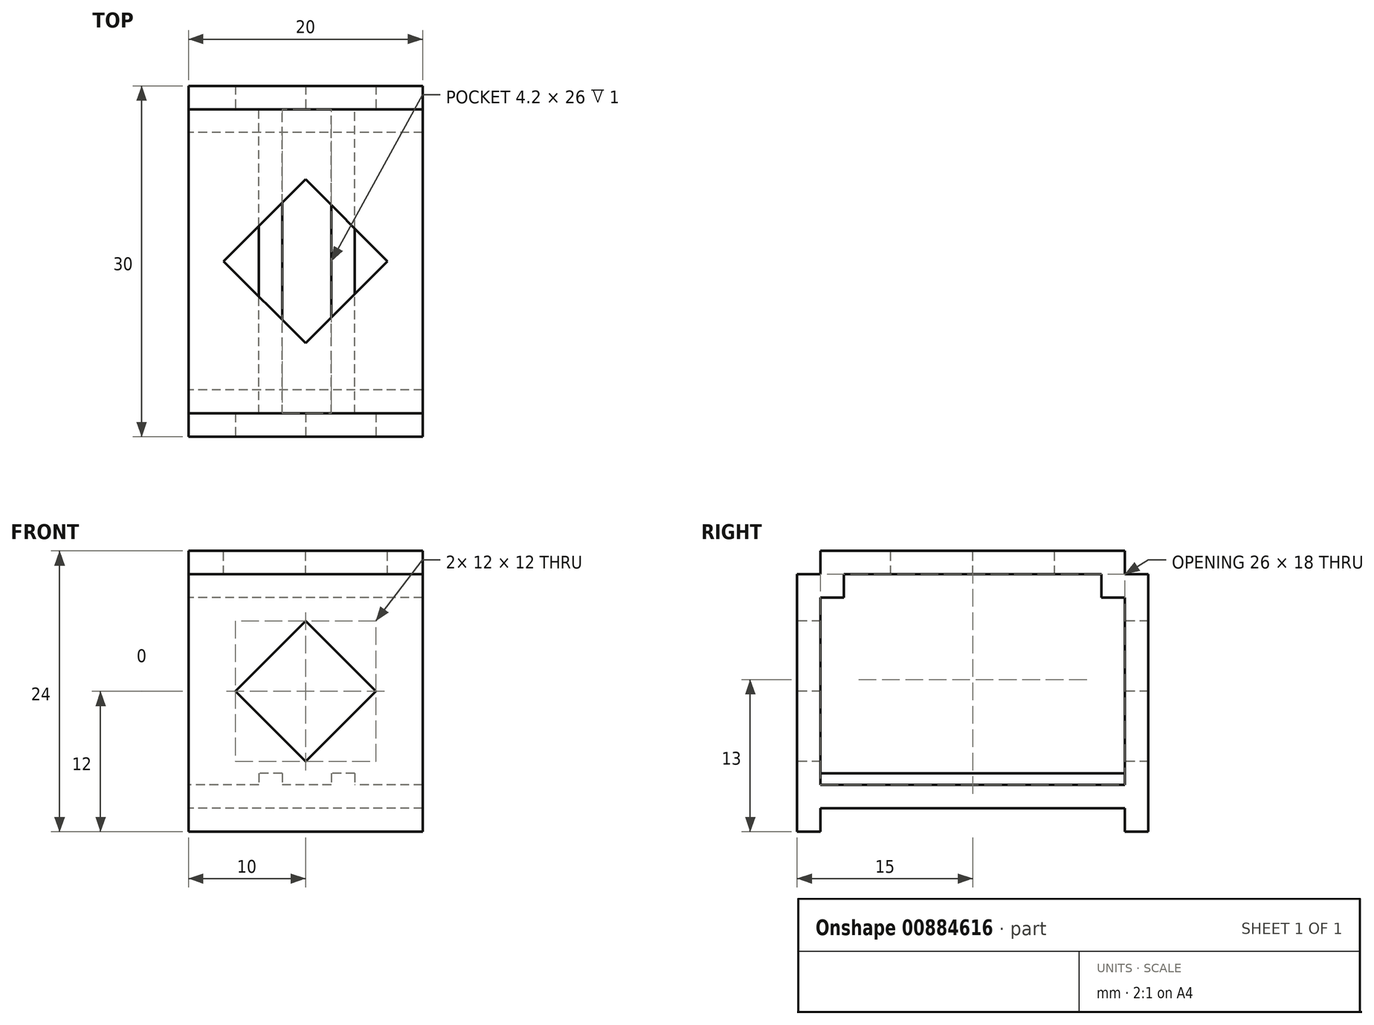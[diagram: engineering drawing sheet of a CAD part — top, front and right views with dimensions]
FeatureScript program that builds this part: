
annotation { "Feature Type Name" : "Feature", "Feature Type Description" : "" }
export const myFeature = defineFeature(function(context is Context, id is Id, definition is map)
    precondition{}
    {
        {
            var Q0;
            Q0=qCreatedBy(makeId("Right.planeOp"),FACE);
            var sketch = newSketch(context, id + "F0", { "sketchPlane" : qUnion([Q0])});
            skLineSegment(sketch, "E0", {"start": v(-13, 0) * mm, "end": v(13, 0) * mm});
            skLineSegment(sketch, "E1", {"start": v(13, 0) * mm, "end": v(13, -2) * mm});
            skLineSegment(sketch, "E2", {"start": v(13, -2) * mm, "end": v(15, -2) * mm});
            skLineSegment(sketch, "E3", {"start": v(15, -2) * mm, "end": v(15, 20) * mm});
            skLineSegment(sketch, "E4", {"start": v(15, 20) * mm, "end": v(13, 20) * mm});
            skLineSegment(sketch, "E5", {"start": v(13, 20) * mm, "end": v(13, 22) * mm});
            skLineSegment(sketch, "E6", {"start": v(13, 22) * mm, "end": v(-13, 22) * mm});
            skLineSegment(sketch, "E7", {"start": v(-13, 22) * mm, "end": v(-13, 20) * mm});
            skLineSegment(sketch, "E8", {"start": v(-13, 20) * mm, "end": v(-15, 20) * mm});
            skLineSegment(sketch, "E9", {"start": v(-15, 20) * mm, "end": v(-15, -2) * mm});
            skLineSegment(sketch, "E10", {"start": v(-15, -2) * mm, "end": v(-13, -2) * mm});
            skLineSegment(sketch, "E11", {"start": v(-13, -2) * mm, "end": v(-13, 0) * mm});
            skSolve(sketch);
        }
        {
            var Q0;
            Q0=makeQuery(id+"F0.imprint","IMPRINT",FACE,{"disambiguationData":[TD([[makeQuery(id+"F0.imprint","IMPRINT",EDGE,{"derivedFrom":sQuery(id+"F0.wireOp",EDGE,"E0")}),1.0]])]});
            extrude(context, id + "F1", {"entities" : qUnion([Q0]), "depth" : 20 * mm, "offsetDistance" : 25 * mm});
        }
        {
            var Q0;
            Q0=makeQuery(id+"F1.opExtrude","CAP_FACE",FACE,{"disambiguationData":[OSD([sQuery(id+"F0.wireOp",EDGE,"E0"),sQuery(id+"F0.wireOp",EDGE,"E1"),sQuery(id+"F0.wireOp",EDGE,"E2"),sQuery(id+"F0.wireOp",EDGE,"E3"),sQuery(id+"F0.wireOp",EDGE,"E4"),sQuery(id+"F0.wireOp",EDGE,"E5"),sQuery(id+"F0.wireOp",EDGE,"E6"),sQuery(id+"F0.wireOp",EDGE,"E7"),sQuery(id+"F0.wireOp",EDGE,"E8"),sQuery(id+"F0.wireOp",EDGE,"E9"),sQuery(id+"F0.wireOp",EDGE,"E10"),sQuery(id+"F0.wireOp",EDGE,"E11")])],"isStart":true});
            var Q1;
            Q1=makeQuery(id+"F1.opExtrude","CAP_FACE",FACE,{"disambiguationData":[OSD([sQuery(id+"F0.wireOp",EDGE,"E0"),sQuery(id+"F0.wireOp",EDGE,"E1"),sQuery(id+"F0.wireOp",EDGE,"E2"),sQuery(id+"F0.wireOp",EDGE,"E3"),sQuery(id+"F0.wireOp",EDGE,"E4"),sQuery(id+"F0.wireOp",EDGE,"E5"),sQuery(id+"F0.wireOp",EDGE,"E6"),sQuery(id+"F0.wireOp",EDGE,"E7"),sQuery(id+"F0.wireOp",EDGE,"E8"),sQuery(id+"F0.wireOp",EDGE,"E9"),sQuery(id+"F0.wireOp",EDGE,"E10"),sQuery(id+"F0.wireOp",EDGE,"E11")])],"isStart":false});
            shell(context, id + "F2", {"entities" : qUnion([Q0, Q1]), "thickness" : 2 * mm});
        }
        {
            var Q0;
            Q0=makeQuery(id+"F2.opShell","OFFSET_FACE",FACE,{"disambiguationData":[OSD([sQuery(id+"F0.wireOp",EDGE,"E3")])]});
            var sketch = newSketch(context, id + "F3", { "sketchPlane" : qUnion([Q0])});
            skLineSegment(sketch, "E12.bottom", {"start": v(8, 3) * mm, "end": v(6, 3) * mm});
            skLineSegment(sketch, "E12.top", {"start": v(8, 2) * mm, "end": v(6, 2) * mm});
            skLineSegment(sketch, "E12.left", {"start": v(8, 3) * mm, "end": v(8, 2) * mm});
            skLineSegment(sketch, "E12.right", {"start": v(6, 3) * mm, "end": v(6, 2) * mm});
            skLineSegment(sketch, "E13.1.0.0", {"start": v(14.2, 3) * mm, "end": v(12.2, 3) * mm});
            skLineSegment(sketch, "E13.1.0.1", {"start": v(14.2, 3) * mm, "end": v(14.2, 2) * mm});
            skLineSegment(sketch, "E13.1.0.2", {"start": v(14.2, 2) * mm, "end": v(12.2, 2) * mm});
            skLineSegment(sketch, "E13.1.0.3", {"start": v(12.2, 3) * mm, "end": v(12.2, 2) * mm});
            skLineSegment(sketch, "E13.direction1", {"start": v(6, 2) * mm, "end": v(12.2, 2) * mm, "construction": true});
            skSolve(sketch);
        }
        {
            var Q0;
            Q0=makeQuery(id+"F3.imprint","IMPRINT",FACE,{"disambiguationData":[TD([[makeQuery(id+"F3.imprint","IMPRINT",EDGE,{"derivedFrom":sQuery(id+"F3.wireOp",EDGE,"E12.bottom")}),1.0]])]});
            var Q1;
            Q1=makeQuery(id+"F3.imprint","IMPRINT",FACE,{"disambiguationData":[TD([[makeQuery(id+"F3.imprint","IMPRINT",EDGE,{"derivedFrom":sQuery(id+"F3.wireOp",EDGE,"E13.1.0.0")}),1.0]])]});
            extrude(context, id + "F4", {"entities" : qUnion([Q0, Q1]), "operationType" : NewBodyOperationType.ADD, "endBound" : BoundingType.UP_TO_NEXT, "depth" : 25 * mm, "offsetDistance" : 25 * mm});
        }
        {
            var Q0;
            Q0=makeQuery(id+"F1.opExtrude","SWEPT_FACE",FACE,{"disambiguationData":[OSD([sQuery(id+"F0.wireOp",EDGE,"E9")])]});
            var sketch = newSketch(context, id + "F5", { "sketchPlane" : qUnion([Q0])});
            skLineSegment(sketch, "E14", {"start": v(10, 16) * mm, "end": v(4, 10) * mm});
            skLineSegment(sketch, "E15", {"start": v(4, 10) * mm, "end": v(10, 4) * mm});
            skLineSegment(sketch, "E16", {"start": v(10, 4) * mm, "end": v(16, 10) * mm});
            skLineSegment(sketch, "E17", {"start": v(16, 10) * mm, "end": v(10, 16) * mm});
            skSolve(sketch);
        }
        {
            var Q0;
            Q0=makeQuery(id+"F5.imprint","IMPRINT",FACE,{"disambiguationData":[TD([[makeQuery(id+"F5.imprint","IMPRINT",EDGE,{"derivedFrom":sQuery(id+"F5.wireOp",EDGE,"E14")}),1.0]])]});
            extrude(context, id + "F6", {"entities" : qUnion([Q0]), "operationType" : NewBodyOperationType.REMOVE, "endBound" : BoundingType.THROUGH_ALL, "oppositeDirection" : true, "depth" : 25 * mm, "offsetDistance" : 25 * mm});
        }
        {
            var Q0;
            Q0=makeQuery(id+"F1.opExtrude","SWEPT_FACE",FACE,{"disambiguationData":[OSD([sQuery(id+"F0.wireOp",EDGE,"E6")])]});
            var sketch = newSketch(context, id + "F7", { "sketchPlane" : qUnion([Q0])});
            skLineSegment(sketch, "E18", {"start": v(10, 7) * mm, "end": v(3, 0) * mm});
            skLineSegment(sketch, "E19", {"start": v(3, 0) * mm, "end": v(10, -7) * mm});
            skLineSegment(sketch, "E20", {"start": v(10, -7) * mm, "end": v(17, 0) * mm});
            skLineSegment(sketch, "E21", {"start": v(17, 0) * mm, "end": v(10, 7) * mm});
            skSolve(sketch);
        }
        {
            var Q0;
            Q0=makeQuery(id+"F7.imprint","IMPRINT",FACE,{"disambiguationData":[TD([[makeQuery(id+"F7.imprint","IMPRINT",EDGE,{"derivedFrom":sQuery(id+"F7.wireOp",EDGE,"E18")}),1.0]])]});
            extrude(context, id + "F8", {"entities" : qUnion([Q0]), "operationType" : NewBodyOperationType.REMOVE, "endBound" : BoundingType.UP_TO_NEXT, "oppositeDirection" : true, "depth" : 25 * mm, "offsetDistance" : 25 * mm});
        }
    });
